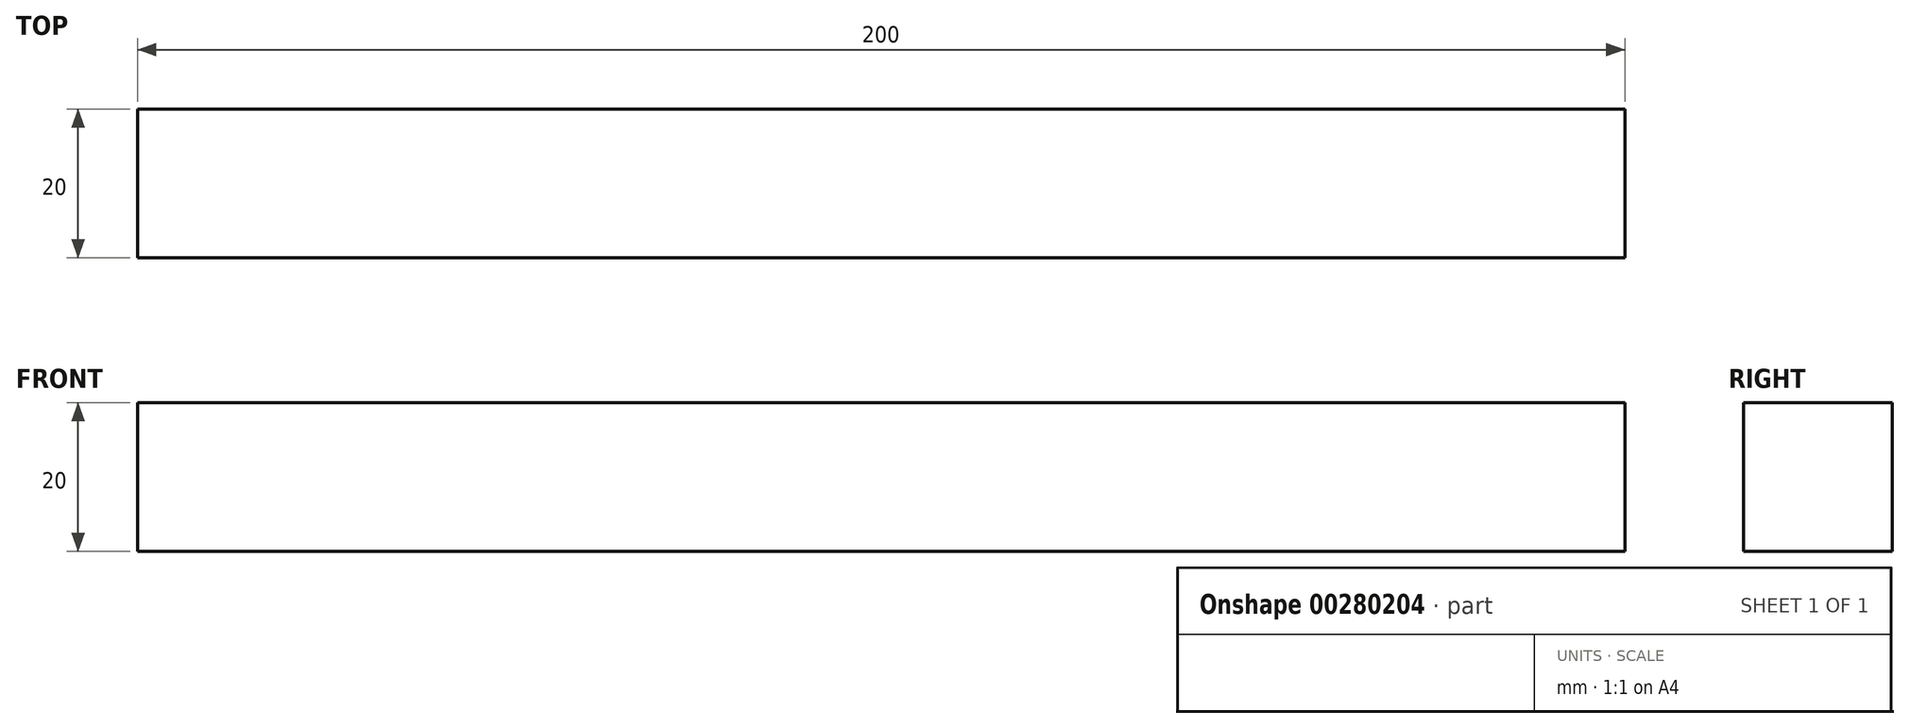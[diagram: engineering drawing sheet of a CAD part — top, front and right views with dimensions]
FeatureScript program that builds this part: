
annotation { "Feature Type Name" : "Feature", "Feature Type Description" : "" }
export const myFeature = defineFeature(function(context is Context, id is Id, definition is map)
    precondition{}
    {
        {
            var Q0;
            Q0=qCreatedBy(makeId("Top.planeOp"),FACE);
            var sketch = newSketch(context, id + "F0", { "sketchPlane" : qUnion([Q0])});
            skLineSegment(sketch, "E0.bottom", {"start": v(-88.88, 0) * mm, "end": v(111.12, 0) * mm});
            skLineSegment(sketch, "E0.top", {"start": v(-88.88, -20) * mm, "end": v(111.12, -20) * mm});
            skLineSegment(sketch, "E0.left", {"start": v(-88.88, 0) * mm, "end": v(-88.88, -20) * mm});
            skLineSegment(sketch, "E0.right", {"start": v(111.12, 0) * mm, "end": v(111.12, -20) * mm});
            skSolve(sketch);
        }
        {
            var Q0;
            Q0 = qSketchRegion(id + "F0", true);
            extrude(context, id + "F1", {"entities" : qUnion([Q0]), "depth" : 20 * mm});
        }
    });
